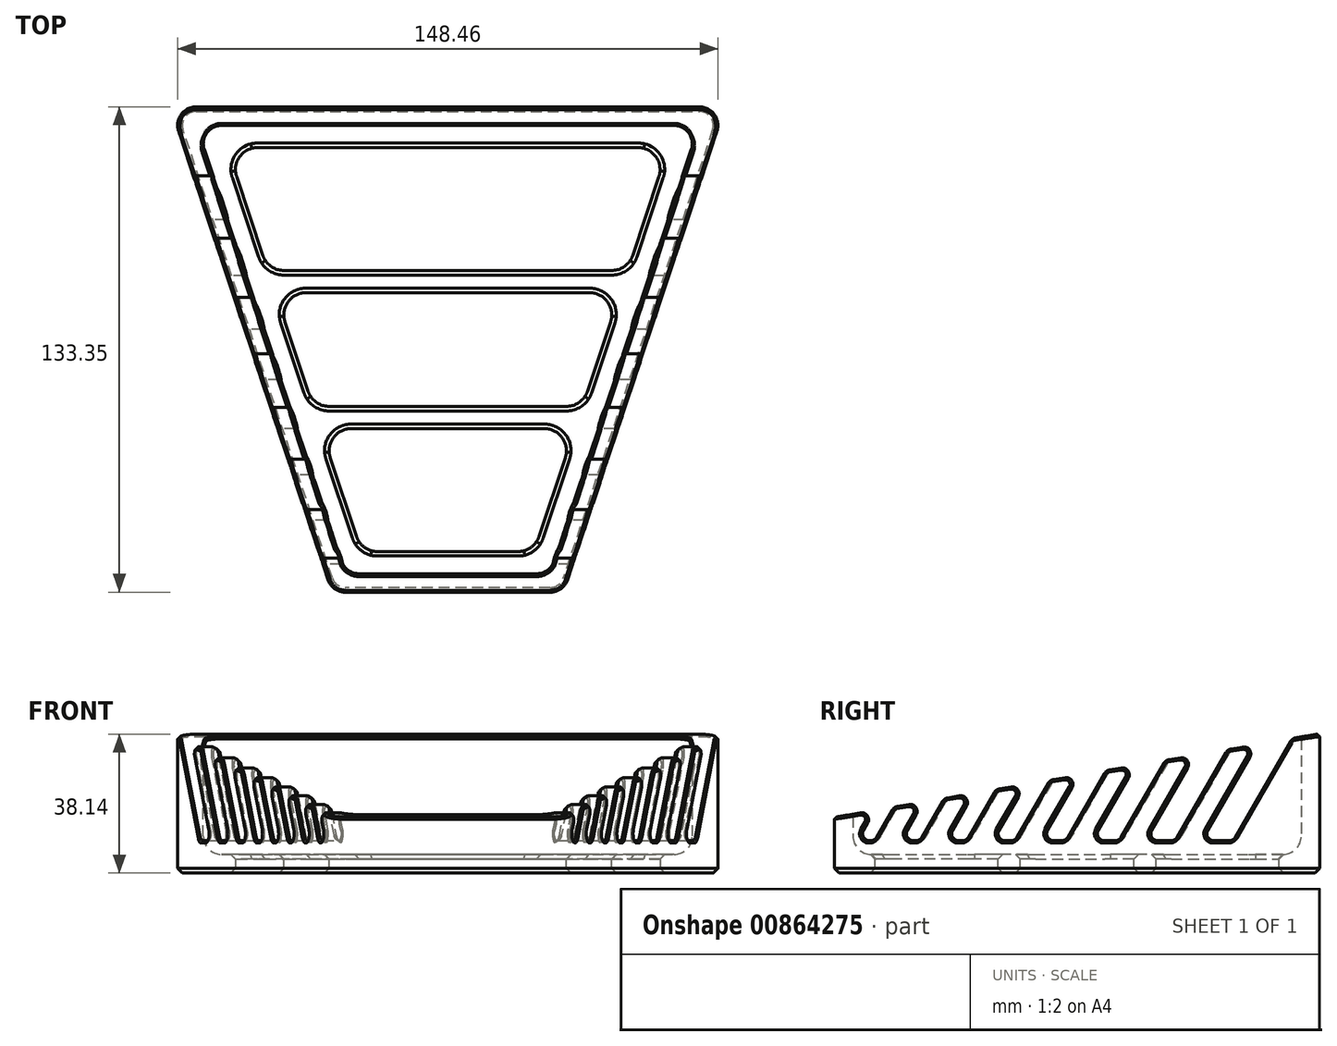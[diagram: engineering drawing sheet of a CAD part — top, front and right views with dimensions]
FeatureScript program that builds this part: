
annotation { "Feature Type Name" : "Feature", "Feature Type Description" : "" }
export const myFeature = defineFeature(function(context is Context, id is Id, definition is map)
    precondition{}
    {
        {
            var Q0;
            Q0=qCreatedBy(makeId("Top.planeOp"),FACE);
            var sketch = newSketch(context, id + "F0", { "sketchPlane" : qUnion([Q0])});
            skLineSegment(sketch, "E0", {"start": v(0, 200.12) * mm, "end": v(0, 0) * mm, "construction": true});
            skLineSegment(sketch, "E1", {"start": v(0, 0) * mm, "end": v(243.38, 0) * mm, "construction": true});
            skLineSegment(sketch, "E2", {"start": v(-76.2, 133.35) * mm, "end": v(76.2, 133.35) * mm});
            skLineSegment(sketch, "E3", {"start": v(76.2, 133.35) * mm, "end": v(31.75, 0) * mm});
            skLineSegment(sketch, "E4", {"start": v(31.75, 0) * mm, "end": v(-31.75, 0) * mm});
            skLineSegment(sketch, "E5", {"start": v(-31.75, 0) * mm, "end": v(-76.2, 133.35) * mm});
            skSolve(sketch);
        }
        {
            var Q0;
            Q0=makeQuery(id+"F0.imprint","IMPRINT",FACE,{"disambiguationData":[TD([[makeQuery(id+"F0.imprint","IMPRINT",EDGE,{"derivedFrom":sQuery(id+"F0.wireOp",EDGE,"E2")}),-1.0]])]});
            extrude(context, id + "F1", {"entities" : qUnion([Q0]), "depth" : 50.8 * mm, "offsetDistance" : 25.4 * mm});
        }
        {
            var Q0;
            Q0=qCreatedBy(makeId("Right.planeOp"),FACE);
            var sketch = newSketch(context, id + "F2", { "sketchPlane" : qUnion([Q0])});
            skLineSegment(sketch, "E6", {"start": v(0, 88.7) * mm, "end": v(0, 0) * mm, "construction": true});
            skLineSegment(sketch, "E7", {"start": v(0, 0) * mm, "end": v(187.78, 0) * mm, "construction": true});
            skCircle(sketch, "E8", {"center": v(118.68, 14.67) * mm, "radius": 14.67 * mm, "construction": true});
            skLineSegment(sketch, "E9", {"start": v(118.68, 14.67) * mm, "end": v(4.95, 4.95) * mm, "construction": true});
            skLineSegment(sketch, "E10", {"start": v(8.28, 1.29) * mm, "end": v(107.5, 5.17) * mm, "construction": true});
            skCircle(sketch, "E11", {"center": v(4.95, 4.95) * mm, "radius": 4.95 * mm, "construction": true});
            skLineSegment(sketch, "E12", {"start": v(116.2, 29.12) * mm, "end": v(4.11, 9.83) * mm, "construction": true});
            skSolve(sketch);
        }
        {
            var Q0;
            Q0=makeQuery(id+"F1.opExtrude","CAP_FACE",FACE,{"disambiguationData":[OSD([sQuery(id+"F0.wireOp",EDGE,"E2"),sQuery(id+"F0.wireOp",EDGE,"E3"),sQuery(id+"F0.wireOp",EDGE,"E4"),sQuery(id+"F0.wireOp",EDGE,"E5")])],"isStart":false});
            shell(context, id + "F3", {"entities" : qUnion([Q0]), "thickness" : 5.08 * mm});
        }
        {
            var Q0;
            Q0=qCreatedBy(makeId("Right.planeOp"),FACE);
            var sketch = newSketch(context, id + "F4", { "sketchPlane" : qUnion([Q0])});
            skLineSegment(sketch, "E13", {"start": v(0, 69.39) * mm, "end": v(0, 0) * mm, "construction": true});
            skLineSegment(sketch, "E14", {"start": v(0, 0) * mm, "end": v(193.07, 0) * mm, "construction": true});
            skLineSegment(sketch, "E15", {"start": v(0, 8.9) * mm, "end": v(186.73, 8.9) * mm, "construction": true});
            skLineSegment(sketch, "E16", {"start": v(-4.36, 14.56) * mm, "end": v(193.37, 48.6) * mm, "construction": true});
            skLineSegment(sketch, "E17", {"start": v(13.77, 17.68) * mm, "end": v(8.7, 8.89) * mm, "construction": true});
            skLineSegment(sketch, "E18", {"start": v(27.37, 20.02) * mm, "end": v(20.94, 8.9) * mm, "construction": true});
            skLineSegment(sketch, "E19", {"start": v(41.37, 22.43) * mm, "end": v(33.55, 8.9) * mm, "construction": true});
            skLineSegment(sketch, "E20", {"start": v(55.86, 24.93) * mm, "end": v(46.6, 8.89) * mm, "construction": true});
            skLineSegment(sketch, "E21", {"start": v(71, 27.53) * mm, "end": v(60.24, 8.89) * mm, "construction": true});
            skLineSegment(sketch, "E22", {"start": v(86.88, 30.27) * mm, "end": v(74.54, 8.89) * mm, "construction": true});
            skLineSegment(sketch, "E23", {"start": v(103.57, 33.14) * mm, "end": v(89.57, 8.89) * mm, "construction": true});
            skLineSegment(sketch, "E24", {"start": v(121, 36.14) * mm, "end": v(105.26, 8.9) * mm, "construction": true});
            skLineSegment(sketch, "E25", {"start": v(125.8, 36.96) * mm, "end": v(146.05, 40.45) * mm});
            skLineSegment(sketch, "E26", {"start": v(146.05, 40.45) * mm, "end": v(146.05, 63.5) * mm});
            skLineSegment(sketch, "E27", {"start": v(146.05, 63.5) * mm, "end": v(-12.7, 63.5) * mm});
            skLineSegment(sketch, "E28", {"start": v(-12.7, 63.5) * mm, "end": v(-12.7, 13.13) * mm});
            skLineSegment(sketch, "E29", {"start": v(-12.7, 13.13) * mm, "end": v(11.17, 17.23) * mm});
            skLineSegment(sketch, "E30", {"start": v(125.8, 36.96) * mm, "end": v(109.59, 8.9) * mm});
            skLineSegment(sketch, "E31", {"start": v(109.59, 8.9) * mm, "end": v(100.94, 8.9) * mm});
            skLineSegment(sketch, "E32", {"start": v(100.94, 8.89) * mm, "end": v(116.2, 35.3) * mm});
            skLineSegment(sketch, "E33", {"start": v(116.2, 35.3) * mm, "end": v(108.05, 33.9) * mm});
            skLineSegment(sketch, "E34", {"start": v(108.05, 33.9) * mm, "end": v(93.6, 8.89) * mm});
            skLineSegment(sketch, "E35", {"start": v(93.6, 8.9) * mm, "end": v(85.54, 8.9) * mm});
            skLineSegment(sketch, "E36", {"start": v(85.54, 8.89) * mm, "end": v(99.1, 32.37) * mm});
            skLineSegment(sketch, "E37", {"start": v(99.1, 32.37) * mm, "end": v(90.95, 30.97) * mm});
            skLineSegment(sketch, "E38", {"start": v(90.95, 30.97) * mm, "end": v(78.2, 8.9) * mm});
            skLineSegment(sketch, "E39", {"start": v(78.2, 8.9) * mm, "end": v(70.87, 8.9) * mm});
            skLineSegment(sketch, "E40", {"start": v(70.87, 8.89) * mm, "end": v(82.81, 29.56) * mm});
            skLineSegment(sketch, "E41", {"start": v(82.81, 29.56) * mm, "end": v(74.67, 28.16) * mm});
            skLineSegment(sketch, "E42", {"start": v(74.67, 28.16) * mm, "end": v(63.54, 8.9) * mm});
            skLineSegment(sketch, "E43", {"start": v(63.54, 8.9) * mm, "end": v(56.94, 8.9) * mm});
            skLineSegment(sketch, "E44", {"start": v(56.94, 8.89) * mm, "end": v(67.34, 26.9) * mm});
            skLineSegment(sketch, "E45", {"start": v(67.34, 26.9) * mm, "end": v(59.2, 25.5) * mm});
            skLineSegment(sketch, "E46", {"start": v(59.2, 25.5) * mm, "end": v(49.61, 8.9) * mm});
            skLineSegment(sketch, "E47", {"start": v(49.61, 8.9) * mm, "end": v(43.6, 8.9) * mm});
            skLineSegment(sketch, "E48", {"start": v(43.6, 8.89) * mm, "end": v(52.53, 24.35) * mm});
            skLineSegment(sketch, "E49", {"start": v(52.53, 24.35) * mm, "end": v(44.38, 22.95) * mm});
            skLineSegment(sketch, "E50", {"start": v(44.38, 22.95) * mm, "end": v(36.27, 8.9) * mm});
            skLineSegment(sketch, "E51", {"start": v(36.27, 8.9) * mm, "end": v(30.84, 8.9) * mm});
            skLineSegment(sketch, "E52", {"start": v(30.84, 8.89) * mm, "end": v(38.36, 21.91) * mm});
            skLineSegment(sketch, "E53", {"start": v(38.36, 21.91) * mm, "end": v(30.22, 20.51) * mm});
            skLineSegment(sketch, "E54", {"start": v(30.22, 20.51) * mm, "end": v(23.5, 8.89) * mm});
            skLineSegment(sketch, "E55", {"start": v(23.5, 8.9) * mm, "end": v(18.38, 8.9) * mm});
            skLineSegment(sketch, "E56", {"start": v(18.38, 8.89) * mm, "end": v(24.52, 19.53) * mm});
            skLineSegment(sketch, "E57", {"start": v(24.52, 19.53) * mm, "end": v(16.38, 18.13) * mm});
            skLineSegment(sketch, "E58", {"start": v(16.38, 18.13) * mm, "end": v(11.04, 8.9) * mm});
            skLineSegment(sketch, "E59", {"start": v(11.04, 8.9) * mm, "end": v(6.35, 8.9) * mm});
            skLineSegment(sketch, "E60", {"start": v(6.35, 8.89) * mm, "end": v(11.17, 17.23) * mm});
            skSolve(sketch);
        }
        {
            var Q0;
            Q0 = qSketchRegion(id + "F4", true);
            extrude(context, id + "F5", {"entities" : qUnion([Q0]), "operationType" : NewBodyOperationType.REMOVE, "endBound" : BoundingType.THROUGH_ALL, "oppositeDirection" : true, "depth" : 25.4 * mm, "offsetDistance" : 25.4 * mm, "hasSecondDirection" : true, "secondDirectionBound" : SecondDirectionBoundingType.THROUGH_ALL, "secondDirectionOppositeDirection" : false, "secondDirectionDepth" : 25.4 * mm});
        }
        {
            var Q0;
            Q0=makeQuery(id+"F3.opShell","OFFSET_FACE",FACE,{"disambiguationData":[OSD([sQuery(id+"F0.wireOp",EDGE,"E2"),sQuery(id+"F0.wireOp",EDGE,"E3"),sQuery(id+"F0.wireOp",EDGE,"E4"),sQuery(id+"F0.wireOp",EDGE,"E5")])]});
            var sketch = newSketch(context, id + "F6", { "sketchPlane" : qUnion([Q0])});
            skLineSegment(sketch, "E61", {"start": v(-151.17, 0) * mm, "end": v(0, 0) * mm, "construction": true});
            skLineSegment(sketch, "E62", {"start": v(0, 0) * mm, "end": v(0, 307.09) * mm, "construction": true});
            skLineSegment(sketch, "E63", {"start": v(-23.7, 11.18) * mm, "end": v(23.7, 11.18) * mm});
            skLineSegment(sketch, "E64", {"start": v(23.7, 11.18) * mm, "end": v(34.96, 44.96) * mm});
            skLineSegment(sketch, "E65", {"start": v(60.7, 122.17) * mm, "end": v(-60.7, 122.17) * mm});
            skLineSegment(sketch, "E66", {"start": v(-60.7, 122.17) * mm, "end": v(-49.43, 88.4) * mm});
            skLineSegment(sketch, "E67", {"start": v(-35.97, 48) * mm, "end": v(35.97, 48) * mm, "construction": true});
            skLineSegment(sketch, "E68", {"start": v(-48.42, 85.34) * mm, "end": v(48.42, 85.34) * mm, "construction": true});
            skLineSegment(sketch, "E69", {"start": v(-34.96, 44.96) * mm, "end": v(34.96, 44.96) * mm});
            skLineSegment(sketch, "E70", {"start": v(-36.99, 51.05) * mm, "end": v(36.99, 51.05) * mm});
            skLineSegment(sketch, "E71", {"start": v(-47.4, 82.3) * mm, "end": v(47.4, 82.3) * mm});
            skLineSegment(sketch, "E72", {"start": v(-49.43, 88.4) * mm, "end": v(49.43, 88.4) * mm});
            skLineSegment(sketch, "E73.trimOffspring", {"start": v(-34.96, 44.96) * mm, "end": v(-23.7, 11.18) * mm});
            skLineSegment(sketch, "E74.trimOffspring", {"start": v(36.99, 51.05) * mm, "end": v(47.4, 82.3) * mm});
            skLineSegment(sketch, "E75.trimOffspring", {"start": v(49.43, 88.4) * mm, "end": v(60.7, 122.17) * mm});
            skLineSegment(sketch, "E76.trimOffspring", {"start": v(-47.4, 82.3) * mm, "end": v(-36.99, 51.05) * mm});
            skSolve(sketch);
        }
        {
            var Q0;
            Q0=makeQuery(id+"F6.imprint","IMPRINT",FACE,{"disambiguationData":[TD([[makeQuery(id+"F6.imprint","IMPRINT",EDGE,{"derivedFrom":sQuery(id+"F6.wireOp",EDGE,"E65")}),1.0]])]});
            var Q1;
            Q1=makeQuery(id+"F6.imprint","IMPRINT",FACE,{"disambiguationData":[TD([[makeQuery(id+"F6.imprint","IMPRINT",EDGE,{"derivedFrom":sQuery(id+"F6.wireOp",EDGE,"E70")}),1.0]])]});
            var Q2;
            Q2=makeQuery(id+"F6.imprint","IMPRINT",FACE,{"disambiguationData":[TD([[makeQuery(id+"F6.imprint","IMPRINT",EDGE,{"derivedFrom":sQuery(id+"F6.wireOp",EDGE,"E63")}),1.0]])]});
            extrude(context, id + "F7", {"entities" : qUnion([Q0, Q1, Q2]), "operationType" : NewBodyOperationType.REMOVE, "endBound" : BoundingType.THROUGH_ALL, "oppositeDirection" : true, "depth" : 25.4 * mm, "offsetDistance" : 25.4 * mm});
        }
        {
            var Q0;
            Q0=makeQuery(id+"F7.boolean.opBoolean","COPY",EDGE,{"derivedFrom":makeQuery(id+"F7.opExtrude","SWEPT_EDGE",EDGE,{"disambiguationData":[OSD([sQuery(id+"F6.wireOp",EDGE,"E65"),sQuery(id+"F6.wireOp",EDGE,"E66")])]})});
            var Q1;
            Q1=makeQuery(id+"F7.boolean.opBoolean","COPY",EDGE,{"derivedFrom":makeQuery(id+"F7.opExtrude","SWEPT_EDGE",EDGE,{"disambiguationData":[OSD([sQuery(id+"F6.wireOp",EDGE,"E65"),sQuery(id+"F6.wireOp",EDGE,"E75.trimOffspring")])]})});
            var Q2;
            Q2=makeQuery(id+"F7.boolean.opBoolean","COPY",EDGE,{"derivedFrom":makeQuery(id+"F7.opExtrude","SWEPT_EDGE",EDGE,{"disambiguationData":[OSD([sQuery(id+"F6.wireOp",EDGE,"E71"),sQuery(id+"F6.wireOp",EDGE,"E74.trimOffspring")])]})});
            var Q3;
            Q3=makeQuery(id+"F7.boolean.opBoolean","COPY",EDGE,{"derivedFrom":makeQuery(id+"F7.opExtrude","SWEPT_EDGE",EDGE,{"disambiguationData":[OSD([sQuery(id+"F6.wireOp",EDGE,"E64"),sQuery(id+"F6.wireOp",EDGE,"E69")])]})});
            var Q4;
            Q4=makeQuery(id+"F7.boolean.opBoolean","COPY",EDGE,{"derivedFrom":makeQuery(id+"F7.opExtrude","SWEPT_EDGE",EDGE,{"disambiguationData":[OSD([sQuery(id+"F6.wireOp",EDGE,"E63"),sQuery(id+"F6.wireOp",EDGE,"E64")])]})});
            var Q5;
            Q5=makeQuery(id+"F7.boolean.opBoolean","COPY",EDGE,{"derivedFrom":makeQuery(id+"F7.opExtrude","SWEPT_EDGE",EDGE,{"disambiguationData":[OSD([sQuery(id+"F6.wireOp",EDGE,"E70"),sQuery(id+"F6.wireOp",EDGE,"E74.trimOffspring")])]})});
            var Q6;
            Q6=makeQuery(id+"F7.boolean.opBoolean","COPY",EDGE,{"derivedFrom":makeQuery(id+"F7.opExtrude","SWEPT_EDGE",EDGE,{"disambiguationData":[OSD([sQuery(id+"F6.wireOp",EDGE,"E72"),sQuery(id+"F6.wireOp",EDGE,"E75.trimOffspring")])]})});
            var Q7;
            Q7=makeQuery(id+"F7.boolean.opBoolean","COPY",EDGE,{"derivedFrom":makeQuery(id+"F7.opExtrude","SWEPT_EDGE",EDGE,{"disambiguationData":[OSD([sQuery(id+"F6.wireOp",EDGE,"E63"),sQuery(id+"F6.wireOp",EDGE,"E73.trimOffspring")])]})});
            var Q8;
            Q8=makeQuery(id+"F7.boolean.opBoolean","COPY",EDGE,{"derivedFrom":makeQuery(id+"F7.opExtrude","SWEPT_EDGE",EDGE,{"disambiguationData":[OSD([sQuery(id+"F6.wireOp",EDGE,"E70"),sQuery(id+"F6.wireOp",EDGE,"E76.trimOffspring")])]})});
            var Q9;
            Q9=makeQuery(id+"F7.boolean.opBoolean","COPY",EDGE,{"derivedFrom":makeQuery(id+"F7.opExtrude","SWEPT_EDGE",EDGE,{"disambiguationData":[OSD([sQuery(id+"F6.wireOp",EDGE,"E66"),sQuery(id+"F6.wireOp",EDGE,"E72")])]})});
            var Q10;
            Q10=makeQuery(id+"F7.boolean.opBoolean","COPY",EDGE,{"derivedFrom":makeQuery(id+"F7.opExtrude","SWEPT_EDGE",EDGE,{"disambiguationData":[OSD([sQuery(id+"F6.wireOp",EDGE,"E71"),sQuery(id+"F6.wireOp",EDGE,"E76.trimOffspring")])]})});
            var Q11;
            Q11=makeQuery(id+"F7.boolean.opBoolean","COPY",EDGE,{"derivedFrom":makeQuery(id+"F7.opExtrude","SWEPT_EDGE",EDGE,{"disambiguationData":[OSD([sQuery(id+"F6.wireOp",EDGE,"E69"),sQuery(id+"F6.wireOp",EDGE,"E73.trimOffspring")])]})});
            fillet(context, id + "F8", {"entities" : qUnion([Q0, Q1, Q2, Q3, Q4, Q5, Q6, Q7, Q8, Q9, Q10, Q11]), "radius" : 6.1 * mm, "tangentPropagation" : true, "allowEdgeOverflow" : false});
        }
        {
            var Q0;
            Q0=makeQuery(id+"F3.opShell","OFFSET_EDGE",EDGE,{"disambiguationData":[OSD([sQuery(id+"F0.wireOp",EDGE,"E2"),sQuery(id+"F0.wireOp",EDGE,"E3")])]});
            var Q1;
            Q1=makeQuery(id+"F3.opShell","OFFSET_EDGE",EDGE,{"disambiguationData":[OSD([sQuery(id+"F0.wireOp",EDGE,"E2"),sQuery(id+"F0.wireOp",EDGE,"E5")])]});
            var Q2;
            Q2=makeQuery(id+"F3.opShell","OFFSET_EDGE",EDGE,{"disambiguationData":[OSD([sQuery(id+"F0.wireOp",EDGE,"E4"),sQuery(id+"F0.wireOp",EDGE,"E5")])]});
            var Q3;
            Q3=makeQuery(id+"F3.opShell","OFFSET_EDGE",EDGE,{"disambiguationData":[OSD([sQuery(id+"F0.wireOp",EDGE,"E3"),sQuery(id+"F0.wireOp",EDGE,"E4")])]});
            var Q4;
            Q4=makeQuery(id+"F1.opExtrude","SWEPT_EDGE",EDGE,{"disambiguationData":[OSD([sQuery(id+"F0.wireOp",EDGE,"E2"),sQuery(id+"F0.wireOp",EDGE,"E5")])]});
            var Q5;
            Q5=makeQuery(id+"F1.opExtrude","SWEPT_EDGE",EDGE,{"disambiguationData":[OSD([sQuery(id+"F0.wireOp",EDGE,"E4"),sQuery(id+"F0.wireOp",EDGE,"E5")])]});
            var Q6;
            Q6=makeQuery(id+"F1.opExtrude","SWEPT_EDGE",EDGE,{"disambiguationData":[OSD([sQuery(id+"F0.wireOp",EDGE,"E3"),sQuery(id+"F0.wireOp",EDGE,"E4")])]});
            var Q7;
            Q7=makeQuery(id+"F1.opExtrude","SWEPT_EDGE",EDGE,{"disambiguationData":[OSD([sQuery(id+"F0.wireOp",EDGE,"E2"),sQuery(id+"F0.wireOp",EDGE,"E3")])]});
            fillet(context, id + "F9", {"entities" : qUnion([Q0, Q1, Q2, Q3, Q4, Q5, Q6, Q7]), "radius" : 5.08 * mm, "tangentPropagation" : true, "allowEdgeOverflow" : false});
        }
        {
            var Q0;
            {var subQ0=sQuery(id+"F0.wireOp",EDGE,"E5");var subQ1=sQuery(id+"F0.wireOp",EDGE,"E2");Q0=makeQuery(id+"F9.opFillet","BLEND_EDGE",EDGE,{"blendedFrom":[makeQuery(id+"F3.opShell","OFFSET_EDGE",EDGE,{"disambiguationData":[OSD([subQ1,subQ0])]}),makeQuery(id+"F3.opShell","OFFSET_FACE",FACE,{"disambiguationData":[OSD([subQ1,sQuery(id+"F0.wireOp",EDGE,"E3"),sQuery(id+"F0.wireOp",EDGE,"E4"),subQ0])]})],"blendedInto":[makeQuery(id+"F3.opShell","OFFSET_FACE",FACE,{"disambiguationData":[OSD([subQ1,sQuery(id+"F0.wireOp",EDGE,"E3"),sQuery(id+"F0.wireOp",EDGE,"E4"),subQ0])]})]});}
            fillet(context, id + "F10", {"entities" : qUnion([Q0]), "radius" : 5.08 * mm, "tangentPropagation" : true, "allowEdgeOverflow" : false});
        }
        {
            var Q0;
            {var subQ0=sQuery(id+"F0.wireOp",EDGE,"E3");var subQ1=sQuery(id+"F4.wireOp",EDGE,"E58");var subQ2=sQuery(id+"F4.wireOp",EDGE,"E59");Q0=makeQuery(id+"F5.boolean.opBoolean","COPY",EDGE,{"disambiguationData":[TD([makeQuery(id+"F1.opExtrude","SWEPT_FACE",FACE,{"disambiguationData":[OSD([subQ0])]})])],"derivedFrom":makeQuery(id+"F5.opExtrude","SWEPT_EDGE",EDGE,{"disambiguationData":[OSD([subQ1,subQ2])]})});}
            var Q1;
            {var subQ0=sQuery(id+"F0.wireOp",EDGE,"E3");var subQ1=sQuery(id+"F4.wireOp",EDGE,"E59");var subQ2=sQuery(id+"F4.wireOp",EDGE,"E60");Q1=makeQuery(id+"F5.boolean.opBoolean","COPY",EDGE,{"disambiguationData":[TD([makeQuery(id+"F1.opExtrude","SWEPT_FACE",FACE,{"disambiguationData":[OSD([subQ0])]})])],"derivedFrom":makeQuery(id+"F5.opExtrude","SWEPT_EDGE",EDGE,{"disambiguationData":[OSD([subQ1,subQ2])]})});}
            var Q2;
            {var subQ0=sQuery(id+"F0.wireOp",EDGE,"E3");var subQ1=sQuery(id+"F4.wireOp",EDGE,"E56");var subQ2=sQuery(id+"F4.wireOp",EDGE,"E55");Q2=makeQuery(id+"F5.boolean.opBoolean","COPY",EDGE,{"disambiguationData":[TD([makeQuery(id+"F1.opExtrude","SWEPT_FACE",FACE,{"disambiguationData":[OSD([subQ0])]})])],"derivedFrom":makeQuery(id+"F5.opExtrude","SWEPT_EDGE",EDGE,{"disambiguationData":[OSD([subQ2,subQ1])]})});}
            var Q3;
            {var subQ0=sQuery(id+"F0.wireOp",EDGE,"E3");var subQ1=sQuery(id+"F4.wireOp",EDGE,"E54");var subQ2=sQuery(id+"F4.wireOp",EDGE,"E55");Q3=makeQuery(id+"F5.boolean.opBoolean","COPY",EDGE,{"disambiguationData":[TD([makeQuery(id+"F1.opExtrude","SWEPT_FACE",FACE,{"disambiguationData":[OSD([subQ0])]})])],"derivedFrom":makeQuery(id+"F5.opExtrude","SWEPT_EDGE",EDGE,{"disambiguationData":[OSD([subQ1,subQ2])]})});}
            var Q4;
            {var subQ0=sQuery(id+"F0.wireOp",EDGE,"E3");var subQ1=sQuery(id+"F4.wireOp",EDGE,"E51");var subQ2=sQuery(id+"F4.wireOp",EDGE,"E50");Q4=makeQuery(id+"F5.boolean.opBoolean","COPY",EDGE,{"disambiguationData":[TD([makeQuery(id+"F1.opExtrude","SWEPT_FACE",FACE,{"disambiguationData":[OSD([subQ0])]})])],"derivedFrom":makeQuery(id+"F5.opExtrude","SWEPT_EDGE",EDGE,{"disambiguationData":[OSD([subQ2,subQ1])]})});}
            var Q5;
            {var subQ0=sQuery(id+"F0.wireOp",EDGE,"E3");var subQ1=sQuery(id+"F4.wireOp",EDGE,"E46");var subQ2=sQuery(id+"F4.wireOp",EDGE,"E47");Q5=makeQuery(id+"F5.boolean.opBoolean","COPY",EDGE,{"disambiguationData":[TD([makeQuery(id+"F1.opExtrude","SWEPT_FACE",FACE,{"disambiguationData":[OSD([subQ0])]})])],"derivedFrom":makeQuery(id+"F5.opExtrude","SWEPT_EDGE",EDGE,{"disambiguationData":[OSD([subQ1,subQ2])]})});}
            var Q6;
            {var subQ0=sQuery(id+"F0.wireOp",EDGE,"E3");var subQ1=sQuery(id+"F4.wireOp",EDGE,"E42");var subQ2=sQuery(id+"F4.wireOp",EDGE,"E43");Q6=makeQuery(id+"F5.boolean.opBoolean","COPY",EDGE,{"disambiguationData":[TD([makeQuery(id+"F1.opExtrude","SWEPT_FACE",FACE,{"disambiguationData":[OSD([subQ0])]})])],"derivedFrom":makeQuery(id+"F5.opExtrude","SWEPT_EDGE",EDGE,{"disambiguationData":[OSD([subQ1,subQ2])]})});}
            var Q7;
            {var subQ0=sQuery(id+"F0.wireOp",EDGE,"E3");var subQ1=sQuery(id+"F4.wireOp",EDGE,"E38");var subQ2=sQuery(id+"F4.wireOp",EDGE,"E39");Q7=makeQuery(id+"F5.boolean.opBoolean","COPY",EDGE,{"disambiguationData":[TD([makeQuery(id+"F1.opExtrude","SWEPT_FACE",FACE,{"disambiguationData":[OSD([subQ0])]})])],"derivedFrom":makeQuery(id+"F5.opExtrude","SWEPT_EDGE",EDGE,{"disambiguationData":[OSD([subQ1,subQ2])]})});}
            var Q8;
            {var subQ0=sQuery(id+"F0.wireOp",EDGE,"E3");var subQ1=sQuery(id+"F4.wireOp",EDGE,"E34");var subQ2=sQuery(id+"F4.wireOp",EDGE,"E35");Q8=makeQuery(id+"F5.boolean.opBoolean","COPY",EDGE,{"disambiguationData":[TD([makeQuery(id+"F1.opExtrude","SWEPT_FACE",FACE,{"disambiguationData":[OSD([subQ0])]})])],"derivedFrom":makeQuery(id+"F5.opExtrude","SWEPT_EDGE",EDGE,{"disambiguationData":[OSD([subQ1,subQ2])]})});}
            var Q9;
            {var subQ0=sQuery(id+"F0.wireOp",EDGE,"E3");var subQ1=sQuery(id+"F4.wireOp",EDGE,"E31");var subQ2=sQuery(id+"F4.wireOp",EDGE,"E30");Q9=makeQuery(id+"F5.boolean.opBoolean","COPY",EDGE,{"disambiguationData":[TD([makeQuery(id+"F1.opExtrude","SWEPT_FACE",FACE,{"disambiguationData":[OSD([subQ0])]})])],"derivedFrom":makeQuery(id+"F5.opExtrude","SWEPT_EDGE",EDGE,{"disambiguationData":[OSD([subQ2,subQ1])]})});}
            var Q10;
            {var subQ0=sQuery(id+"F0.wireOp",EDGE,"E3");var subQ1=sQuery(id+"F4.wireOp",EDGE,"E31");var subQ2=sQuery(id+"F4.wireOp",EDGE,"E32");Q10=makeQuery(id+"F5.boolean.opBoolean","COPY",EDGE,{"disambiguationData":[TD([makeQuery(id+"F1.opExtrude","SWEPT_FACE",FACE,{"disambiguationData":[OSD([subQ0])]})])],"derivedFrom":makeQuery(id+"F5.opExtrude","SWEPT_EDGE",EDGE,{"disambiguationData":[OSD([subQ1,subQ2])]})});}
            var Q11;
            {var subQ0=sQuery(id+"F0.wireOp",EDGE,"E3");var subQ1=sQuery(id+"F4.wireOp",EDGE,"E36");var subQ2=sQuery(id+"F4.wireOp",EDGE,"E35");Q11=makeQuery(id+"F5.boolean.opBoolean","COPY",EDGE,{"disambiguationData":[TD([makeQuery(id+"F1.opExtrude","SWEPT_FACE",FACE,{"disambiguationData":[OSD([subQ0])]})])],"derivedFrom":makeQuery(id+"F5.opExtrude","SWEPT_EDGE",EDGE,{"disambiguationData":[OSD([subQ2,subQ1])]})});}
            var Q12;
            {var subQ0=sQuery(id+"F0.wireOp",EDGE,"E3");var subQ1=sQuery(id+"F4.wireOp",EDGE,"E39");var subQ2=sQuery(id+"F4.wireOp",EDGE,"E40");Q12=makeQuery(id+"F5.boolean.opBoolean","COPY",EDGE,{"disambiguationData":[TD([makeQuery(id+"F1.opExtrude","SWEPT_FACE",FACE,{"disambiguationData":[OSD([subQ0])]})])],"derivedFrom":makeQuery(id+"F5.opExtrude","SWEPT_EDGE",EDGE,{"disambiguationData":[OSD([subQ1,subQ2])]})});}
            var Q13;
            {var subQ0=sQuery(id+"F0.wireOp",EDGE,"E3");var subQ1=sQuery(id+"F4.wireOp",EDGE,"E43");var subQ2=sQuery(id+"F4.wireOp",EDGE,"E44");Q13=makeQuery(id+"F5.boolean.opBoolean","COPY",EDGE,{"disambiguationData":[TD([makeQuery(id+"F1.opExtrude","SWEPT_FACE",FACE,{"disambiguationData":[OSD([subQ0])]})])],"derivedFrom":makeQuery(id+"F5.opExtrude","SWEPT_EDGE",EDGE,{"disambiguationData":[OSD([subQ1,subQ2])]})});}
            var Q14;
            {var subQ0=sQuery(id+"F0.wireOp",EDGE,"E3");var subQ1=sQuery(id+"F4.wireOp",EDGE,"E47");var subQ2=sQuery(id+"F4.wireOp",EDGE,"E48");Q14=makeQuery(id+"F5.boolean.opBoolean","COPY",EDGE,{"disambiguationData":[TD([makeQuery(id+"F1.opExtrude","SWEPT_FACE",FACE,{"disambiguationData":[OSD([subQ0])]})])],"derivedFrom":makeQuery(id+"F5.opExtrude","SWEPT_EDGE",EDGE,{"disambiguationData":[OSD([subQ1,subQ2])]})});}
            var Q15;
            {var subQ0=sQuery(id+"F0.wireOp",EDGE,"E3");var subQ1=sQuery(id+"F4.wireOp",EDGE,"E51");var subQ2=sQuery(id+"F4.wireOp",EDGE,"E52");Q15=makeQuery(id+"F5.boolean.opBoolean","COPY",EDGE,{"disambiguationData":[TD([makeQuery(id+"F1.opExtrude","SWEPT_FACE",FACE,{"disambiguationData":[OSD([subQ0])]})])],"derivedFrom":makeQuery(id+"F5.opExtrude","SWEPT_EDGE",EDGE,{"disambiguationData":[OSD([subQ1,subQ2])]})});}
            var Q16;
            {var subQ0=sQuery(id+"F0.wireOp",EDGE,"E5");var subQ1=sQuery(id+"F4.wireOp",EDGE,"E59");var subQ2=sQuery(id+"F4.wireOp",EDGE,"E60");Q16=makeQuery(id+"F5.boolean.opBoolean","COPY",EDGE,{"disambiguationData":[TD([makeQuery(id+"F1.opExtrude","SWEPT_FACE",FACE,{"disambiguationData":[OSD([subQ0])]})])],"derivedFrom":makeQuery(id+"F5.opExtrude","SWEPT_EDGE",EDGE,{"disambiguationData":[OSD([subQ1,subQ2])]})});}
            var Q17;
            {var subQ0=sQuery(id+"F0.wireOp",EDGE,"E5");var subQ1=sQuery(id+"F4.wireOp",EDGE,"E55");var subQ2=sQuery(id+"F4.wireOp",EDGE,"E56");Q17=makeQuery(id+"F5.boolean.opBoolean","COPY",EDGE,{"disambiguationData":[TD([makeQuery(id+"F1.opExtrude","SWEPT_FACE",FACE,{"disambiguationData":[OSD([subQ0])]})])],"derivedFrom":makeQuery(id+"F5.opExtrude","SWEPT_EDGE",EDGE,{"disambiguationData":[OSD([subQ1,subQ2])]})});}
            var Q18;
            {var subQ0=sQuery(id+"F0.wireOp",EDGE,"E5");var subQ1=sQuery(id+"F4.wireOp",EDGE,"E51");var subQ2=sQuery(id+"F4.wireOp",EDGE,"E52");Q18=makeQuery(id+"F5.boolean.opBoolean","COPY",EDGE,{"disambiguationData":[TD([makeQuery(id+"F1.opExtrude","SWEPT_FACE",FACE,{"disambiguationData":[OSD([subQ0])]})])],"derivedFrom":makeQuery(id+"F5.opExtrude","SWEPT_EDGE",EDGE,{"disambiguationData":[OSD([subQ1,subQ2])]})});}
            var Q19;
            {var subQ0=sQuery(id+"F0.wireOp",EDGE,"E5");var subQ1=sQuery(id+"F4.wireOp",EDGE,"E48");var subQ2=sQuery(id+"F4.wireOp",EDGE,"E47");Q19=makeQuery(id+"F5.boolean.opBoolean","COPY",EDGE,{"disambiguationData":[TD([makeQuery(id+"F1.opExtrude","SWEPT_FACE",FACE,{"disambiguationData":[OSD([subQ0])]})])],"derivedFrom":makeQuery(id+"F5.opExtrude","SWEPT_EDGE",EDGE,{"disambiguationData":[OSD([subQ2,subQ1])]})});}
            var Q20;
            {var subQ0=sQuery(id+"F0.wireOp",EDGE,"E5");var subQ1=sQuery(id+"F4.wireOp",EDGE,"E58");var subQ2=sQuery(id+"F4.wireOp",EDGE,"E59");Q20=makeQuery(id+"F5.boolean.opBoolean","COPY",EDGE,{"disambiguationData":[TD([makeQuery(id+"F1.opExtrude","SWEPT_FACE",FACE,{"disambiguationData":[OSD([subQ0])]})])],"derivedFrom":makeQuery(id+"F5.opExtrude","SWEPT_EDGE",EDGE,{"disambiguationData":[OSD([subQ1,subQ2])]})});}
            var Q21;
            {var subQ0=sQuery(id+"F0.wireOp",EDGE,"E5");var subQ1=sQuery(id+"F4.wireOp",EDGE,"E54");var subQ2=sQuery(id+"F4.wireOp",EDGE,"E55");Q21=makeQuery(id+"F5.boolean.opBoolean","COPY",EDGE,{"disambiguationData":[TD([makeQuery(id+"F1.opExtrude","SWEPT_FACE",FACE,{"disambiguationData":[OSD([subQ0])]})])],"derivedFrom":makeQuery(id+"F5.opExtrude","SWEPT_EDGE",EDGE,{"disambiguationData":[OSD([subQ1,subQ2])]})});}
            var Q22;
            {var subQ0=sQuery(id+"F0.wireOp",EDGE,"E5");var subQ1=sQuery(id+"F4.wireOp",EDGE,"E50");var subQ2=sQuery(id+"F4.wireOp",EDGE,"E51");Q22=makeQuery(id+"F5.boolean.opBoolean","COPY",EDGE,{"disambiguationData":[TD([makeQuery(id+"F1.opExtrude","SWEPT_FACE",FACE,{"disambiguationData":[OSD([subQ0])]})])],"derivedFrom":makeQuery(id+"F5.opExtrude","SWEPT_EDGE",EDGE,{"disambiguationData":[OSD([subQ1,subQ2])]})});}
            var Q23;
            {var subQ0=sQuery(id+"F0.wireOp",EDGE,"E5");var subQ1=sQuery(id+"F4.wireOp",EDGE,"E46");var subQ2=sQuery(id+"F4.wireOp",EDGE,"E47");Q23=makeQuery(id+"F5.boolean.opBoolean","COPY",EDGE,{"disambiguationData":[TD([makeQuery(id+"F1.opExtrude","SWEPT_FACE",FACE,{"disambiguationData":[OSD([subQ0])]})])],"derivedFrom":makeQuery(id+"F5.opExtrude","SWEPT_EDGE",EDGE,{"disambiguationData":[OSD([subQ1,subQ2])]})});}
            var Q24;
            {var subQ0=sQuery(id+"F0.wireOp",EDGE,"E5");var subQ1=sQuery(id+"F4.wireOp",EDGE,"E43");var subQ2=sQuery(id+"F4.wireOp",EDGE,"E42");Q24=makeQuery(id+"F5.boolean.opBoolean","COPY",EDGE,{"disambiguationData":[TD([makeQuery(id+"F1.opExtrude","SWEPT_FACE",FACE,{"disambiguationData":[OSD([subQ0])]})])],"derivedFrom":makeQuery(id+"F5.opExtrude","SWEPT_EDGE",EDGE,{"disambiguationData":[OSD([subQ2,subQ1])]})});}
            var Q25;
            {var subQ0=sQuery(id+"F0.wireOp",EDGE,"E5");var subQ1=sQuery(id+"F4.wireOp",EDGE,"E43");var subQ2=sQuery(id+"F4.wireOp",EDGE,"E44");Q25=makeQuery(id+"F5.boolean.opBoolean","COPY",EDGE,{"disambiguationData":[TD([makeQuery(id+"F1.opExtrude","SWEPT_FACE",FACE,{"disambiguationData":[OSD([subQ0])]})])],"derivedFrom":makeQuery(id+"F5.opExtrude","SWEPT_EDGE",EDGE,{"disambiguationData":[OSD([subQ1,subQ2])]})});}
            var Q26;
            {var subQ0=sQuery(id+"F0.wireOp",EDGE,"E5");var subQ1=sQuery(id+"F4.wireOp",EDGE,"E39");var subQ2=sQuery(id+"F4.wireOp",EDGE,"E40");Q26=makeQuery(id+"F5.boolean.opBoolean","COPY",EDGE,{"disambiguationData":[TD([makeQuery(id+"F1.opExtrude","SWEPT_FACE",FACE,{"disambiguationData":[OSD([subQ0])]})])],"derivedFrom":makeQuery(id+"F5.opExtrude","SWEPT_EDGE",EDGE,{"disambiguationData":[OSD([subQ1,subQ2])]})});}
            var Q27;
            {var subQ0=sQuery(id+"F0.wireOp",EDGE,"E5");var subQ1=sQuery(id+"F4.wireOp",EDGE,"E38");var subQ2=sQuery(id+"F4.wireOp",EDGE,"E39");Q27=makeQuery(id+"F5.boolean.opBoolean","COPY",EDGE,{"disambiguationData":[TD([makeQuery(id+"F1.opExtrude","SWEPT_FACE",FACE,{"disambiguationData":[OSD([subQ0])]})])],"derivedFrom":makeQuery(id+"F5.opExtrude","SWEPT_EDGE",EDGE,{"disambiguationData":[OSD([subQ1,subQ2])]})});}
            var Q28;
            {var subQ0=sQuery(id+"F0.wireOp",EDGE,"E5");var subQ1=sQuery(id+"F4.wireOp",EDGE,"E35");var subQ2=sQuery(id+"F4.wireOp",EDGE,"E36");Q28=makeQuery(id+"F5.boolean.opBoolean","COPY",EDGE,{"disambiguationData":[TD([makeQuery(id+"F1.opExtrude","SWEPT_FACE",FACE,{"disambiguationData":[OSD([subQ0])]})])],"derivedFrom":makeQuery(id+"F5.opExtrude","SWEPT_EDGE",EDGE,{"disambiguationData":[OSD([subQ1,subQ2])]})});}
            var Q29;
            {var subQ0=sQuery(id+"F0.wireOp",EDGE,"E5");var subQ1=sQuery(id+"F4.wireOp",EDGE,"E34");var subQ2=sQuery(id+"F4.wireOp",EDGE,"E35");Q29=makeQuery(id+"F5.boolean.opBoolean","COPY",EDGE,{"disambiguationData":[TD([makeQuery(id+"F1.opExtrude","SWEPT_FACE",FACE,{"disambiguationData":[OSD([subQ0])]})])],"derivedFrom":makeQuery(id+"F5.opExtrude","SWEPT_EDGE",EDGE,{"disambiguationData":[OSD([subQ1,subQ2])]})});}
            var Q30;
            {var subQ0=sQuery(id+"F0.wireOp",EDGE,"E5");var subQ1=sQuery(id+"F4.wireOp",EDGE,"E30");var subQ2=sQuery(id+"F4.wireOp",EDGE,"E31");Q30=makeQuery(id+"F5.boolean.opBoolean","COPY",EDGE,{"disambiguationData":[TD([makeQuery(id+"F1.opExtrude","SWEPT_FACE",FACE,{"disambiguationData":[OSD([subQ0])]})])],"derivedFrom":makeQuery(id+"F5.opExtrude","SWEPT_EDGE",EDGE,{"disambiguationData":[OSD([subQ1,subQ2])]})});}
            var Q31;
            {var subQ0=sQuery(id+"F0.wireOp",EDGE,"E5");var subQ1=sQuery(id+"F4.wireOp",EDGE,"E31");var subQ2=sQuery(id+"F4.wireOp",EDGE,"E32");Q31=makeQuery(id+"F5.boolean.opBoolean","COPY",EDGE,{"disambiguationData":[TD([makeQuery(id+"F1.opExtrude","SWEPT_FACE",FACE,{"disambiguationData":[OSD([subQ0])]})])],"derivedFrom":makeQuery(id+"F5.opExtrude","SWEPT_EDGE",EDGE,{"disambiguationData":[OSD([subQ1,subQ2])]})});}
            fillet(context, id + "F11", {"entities" : qUnion([Q0, Q1, Q2, Q3, Q4, Q5, Q6, Q7, Q8, Q9, Q10, Q11, Q12, Q13, Q14, Q15, Q16, Q17, Q18, Q19, Q20, Q21, Q22, Q23, Q24, Q25, Q26, Q27, Q28, Q29, Q30, Q31]), "radius" : 1.9 * mm, "tangentPropagation" : true, "allowEdgeOverflow" : false});
        }
        {
            var Q0;
            {var subQ0=sQuery(id+"F0.wireOp",EDGE,"E3");var subQ1=sQuery(id+"F4.wireOp",EDGE,"E29");var subQ2=sQuery(id+"F4.wireOp",EDGE,"E60");Q0=makeQuery(id+"F5.boolean.opBoolean","COPY",EDGE,{"disambiguationData":[TD([makeQuery(id+"F1.opExtrude","SWEPT_FACE",FACE,{"disambiguationData":[OSD([subQ0])]})])],"derivedFrom":makeQuery(id+"F5.opExtrude","SWEPT_EDGE",EDGE,{"disambiguationData":[OSD([subQ1,subQ2])]})});}
            var Q1;
            {var subQ0=sQuery(id+"F0.wireOp",EDGE,"E3");var subQ1=sQuery(id+"F4.wireOp",EDGE,"E57");var subQ2=sQuery(id+"F4.wireOp",EDGE,"E58");Q1=makeQuery(id+"F5.boolean.opBoolean","COPY",EDGE,{"disambiguationData":[TD([makeQuery(id+"F1.opExtrude","SWEPT_FACE",FACE,{"disambiguationData":[OSD([subQ0])]})])],"derivedFrom":makeQuery(id+"F5.opExtrude","SWEPT_EDGE",EDGE,{"disambiguationData":[OSD([subQ1,subQ2])]})});}
            var Q2;
            {var subQ0=sQuery(id+"F0.wireOp",EDGE,"E5");var subQ1=sQuery(id+"F4.wireOp",EDGE,"E29");var subQ2=sQuery(id+"F4.wireOp",EDGE,"E60");Q2=makeQuery(id+"F5.boolean.opBoolean","COPY",EDGE,{"disambiguationData":[TD([makeQuery(id+"F1.opExtrude","SWEPT_FACE",FACE,{"disambiguationData":[OSD([subQ0])]})])],"derivedFrom":makeQuery(id+"F5.opExtrude","SWEPT_EDGE",EDGE,{"disambiguationData":[OSD([subQ1,subQ2])]})});}
            var Q3;
            {var subQ0=sQuery(id+"F0.wireOp",EDGE,"E5");var subQ1=sQuery(id+"F4.wireOp",EDGE,"E58");var subQ2=sQuery(id+"F4.wireOp",EDGE,"E57");Q3=makeQuery(id+"F5.boolean.opBoolean","COPY",EDGE,{"disambiguationData":[TD([makeQuery(id+"F1.opExtrude","SWEPT_FACE",FACE,{"disambiguationData":[OSD([subQ0])]})])],"derivedFrom":makeQuery(id+"F5.opExtrude","SWEPT_EDGE",EDGE,{"disambiguationData":[OSD([subQ2,subQ1])]})});}
            var Q4;
            {var subQ0=sQuery(id+"F0.wireOp",EDGE,"E5");var subQ1=sQuery(id+"F4.wireOp",EDGE,"E56");var subQ2=sQuery(id+"F4.wireOp",EDGE,"E57");Q4=makeQuery(id+"F5.boolean.opBoolean","COPY",EDGE,{"disambiguationData":[TD([makeQuery(id+"F1.opExtrude","SWEPT_FACE",FACE,{"disambiguationData":[OSD([subQ0])]})])],"derivedFrom":makeQuery(id+"F5.opExtrude","SWEPT_EDGE",EDGE,{"disambiguationData":[OSD([subQ1,subQ2])]})});}
            var Q5;
            {var subQ0=sQuery(id+"F0.wireOp",EDGE,"E5");var subQ1=sQuery(id+"F4.wireOp",EDGE,"E53");var subQ2=sQuery(id+"F4.wireOp",EDGE,"E54");Q5=makeQuery(id+"F5.boolean.opBoolean","COPY",EDGE,{"disambiguationData":[TD([makeQuery(id+"F1.opExtrude","SWEPT_FACE",FACE,{"disambiguationData":[OSD([subQ0])]})])],"derivedFrom":makeQuery(id+"F5.opExtrude","SWEPT_EDGE",EDGE,{"disambiguationData":[OSD([subQ1,subQ2])]})});}
            var Q6;
            {var subQ0=sQuery(id+"F0.wireOp",EDGE,"E5");var subQ1=sQuery(id+"F4.wireOp",EDGE,"E53");var subQ2=sQuery(id+"F4.wireOp",EDGE,"E52");Q6=makeQuery(id+"F5.boolean.opBoolean","COPY",EDGE,{"disambiguationData":[TD([makeQuery(id+"F1.opExtrude","SWEPT_FACE",FACE,{"disambiguationData":[OSD([subQ0])]})])],"derivedFrom":makeQuery(id+"F5.opExtrude","SWEPT_EDGE",EDGE,{"disambiguationData":[OSD([subQ2,subQ1])]})});}
            var Q7;
            {var subQ0=sQuery(id+"F0.wireOp",EDGE,"E5");var subQ1=sQuery(id+"F4.wireOp",EDGE,"E49");var subQ2=sQuery(id+"F4.wireOp",EDGE,"E50");Q7=makeQuery(id+"F5.boolean.opBoolean","COPY",EDGE,{"disambiguationData":[TD([makeQuery(id+"F1.opExtrude","SWEPT_FACE",FACE,{"disambiguationData":[OSD([subQ0])]})])],"derivedFrom":makeQuery(id+"F5.opExtrude","SWEPT_EDGE",EDGE,{"disambiguationData":[OSD([subQ1,subQ2])]})});}
            var Q8;
            {var subQ0=sQuery(id+"F0.wireOp",EDGE,"E5");var subQ1=sQuery(id+"F4.wireOp",EDGE,"E48");var subQ2=sQuery(id+"F4.wireOp",EDGE,"E49");Q8=makeQuery(id+"F5.boolean.opBoolean","COPY",EDGE,{"disambiguationData":[TD([makeQuery(id+"F1.opExtrude","SWEPT_FACE",FACE,{"disambiguationData":[OSD([subQ0])]})])],"derivedFrom":makeQuery(id+"F5.opExtrude","SWEPT_EDGE",EDGE,{"disambiguationData":[OSD([subQ1,subQ2])]})});}
            var Q9;
            {var subQ0=sQuery(id+"F0.wireOp",EDGE,"E5");var subQ1=sQuery(id+"F4.wireOp",EDGE,"E45");var subQ2=sQuery(id+"F4.wireOp",EDGE,"E46");Q9=makeQuery(id+"F5.boolean.opBoolean","COPY",EDGE,{"disambiguationData":[TD([makeQuery(id+"F1.opExtrude","SWEPT_FACE",FACE,{"disambiguationData":[OSD([subQ0])]})])],"derivedFrom":makeQuery(id+"F5.opExtrude","SWEPT_EDGE",EDGE,{"disambiguationData":[OSD([subQ1,subQ2])]})});}
            var Q10;
            {var subQ0=sQuery(id+"F0.wireOp",EDGE,"E5");var subQ1=sQuery(id+"F4.wireOp",EDGE,"E44");var subQ2=sQuery(id+"F4.wireOp",EDGE,"E45");Q10=makeQuery(id+"F5.boolean.opBoolean","COPY",EDGE,{"disambiguationData":[TD([makeQuery(id+"F1.opExtrude","SWEPT_FACE",FACE,{"disambiguationData":[OSD([subQ0])]})])],"derivedFrom":makeQuery(id+"F5.opExtrude","SWEPT_EDGE",EDGE,{"disambiguationData":[OSD([subQ1,subQ2])]})});}
            var Q11;
            {var subQ0=sQuery(id+"F0.wireOp",EDGE,"E5");var subQ1=sQuery(id+"F4.wireOp",EDGE,"E41");var subQ2=sQuery(id+"F4.wireOp",EDGE,"E42");Q11=makeQuery(id+"F5.boolean.opBoolean","COPY",EDGE,{"disambiguationData":[TD([makeQuery(id+"F1.opExtrude","SWEPT_FACE",FACE,{"disambiguationData":[OSD([subQ0])]})])],"derivedFrom":makeQuery(id+"F5.opExtrude","SWEPT_EDGE",EDGE,{"disambiguationData":[OSD([subQ1,subQ2])]})});}
            var Q12;
            {var subQ0=sQuery(id+"F0.wireOp",EDGE,"E5");var subQ1=sQuery(id+"F4.wireOp",EDGE,"E40");var subQ2=sQuery(id+"F4.wireOp",EDGE,"E41");Q12=makeQuery(id+"F5.boolean.opBoolean","COPY",EDGE,{"disambiguationData":[TD([makeQuery(id+"F1.opExtrude","SWEPT_FACE",FACE,{"disambiguationData":[OSD([subQ0])]})])],"derivedFrom":makeQuery(id+"F5.opExtrude","SWEPT_EDGE",EDGE,{"disambiguationData":[OSD([subQ1,subQ2])]})});}
            var Q13;
            {var subQ0=sQuery(id+"F0.wireOp",EDGE,"E5");var subQ1=sQuery(id+"F4.wireOp",EDGE,"E38");var subQ2=sQuery(id+"F4.wireOp",EDGE,"E37");Q13=makeQuery(id+"F5.boolean.opBoolean","COPY",EDGE,{"disambiguationData":[TD([makeQuery(id+"F1.opExtrude","SWEPT_FACE",FACE,{"disambiguationData":[OSD([subQ0])]})])],"derivedFrom":makeQuery(id+"F5.opExtrude","SWEPT_EDGE",EDGE,{"disambiguationData":[OSD([subQ2,subQ1])]})});}
            var Q14;
            {var subQ0=sQuery(id+"F0.wireOp",EDGE,"E5");var subQ1=sQuery(id+"F4.wireOp",EDGE,"E36");var subQ2=sQuery(id+"F4.wireOp",EDGE,"E37");Q14=makeQuery(id+"F5.boolean.opBoolean","COPY",EDGE,{"disambiguationData":[TD([makeQuery(id+"F1.opExtrude","SWEPT_FACE",FACE,{"disambiguationData":[OSD([subQ0])]})])],"derivedFrom":makeQuery(id+"F5.opExtrude","SWEPT_EDGE",EDGE,{"disambiguationData":[OSD([subQ1,subQ2])]})});}
            var Q15;
            {var subQ0=sQuery(id+"F0.wireOp",EDGE,"E5");var subQ1=sQuery(id+"F4.wireOp",EDGE,"E33");var subQ2=sQuery(id+"F4.wireOp",EDGE,"E34");Q15=makeQuery(id+"F5.boolean.opBoolean","COPY",EDGE,{"disambiguationData":[TD([makeQuery(id+"F1.opExtrude","SWEPT_FACE",FACE,{"disambiguationData":[OSD([subQ0])]})])],"derivedFrom":makeQuery(id+"F5.opExtrude","SWEPT_EDGE",EDGE,{"disambiguationData":[OSD([subQ1,subQ2])]})});}
            var Q16;
            {var subQ0=sQuery(id+"F0.wireOp",EDGE,"E5");var subQ1=sQuery(id+"F4.wireOp",EDGE,"E33");var subQ2=sQuery(id+"F4.wireOp",EDGE,"E32");Q16=makeQuery(id+"F5.boolean.opBoolean","COPY",EDGE,{"disambiguationData":[TD([makeQuery(id+"F1.opExtrude","SWEPT_FACE",FACE,{"disambiguationData":[OSD([subQ0])]})])],"derivedFrom":makeQuery(id+"F5.opExtrude","SWEPT_EDGE",EDGE,{"disambiguationData":[OSD([subQ2,subQ1])]})});}
            var Q17;
            {var subQ0=sQuery(id+"F0.wireOp",EDGE,"E5");var subQ1=sQuery(id+"F4.wireOp",EDGE,"E25");var subQ2=sQuery(id+"F4.wireOp",EDGE,"E30");Q17=makeQuery(id+"F5.boolean.opBoolean","COPY",EDGE,{"disambiguationData":[TD([makeQuery(id+"F1.opExtrude","SWEPT_FACE",FACE,{"disambiguationData":[OSD([subQ0])]})])],"derivedFrom":makeQuery(id+"F5.opExtrude","SWEPT_EDGE",EDGE,{"disambiguationData":[OSD([subQ1,subQ2])]})});}
            var Q18;
            {var subQ0=sQuery(id+"F0.wireOp",EDGE,"E3");var subQ1=sQuery(id+"F4.wireOp",EDGE,"E25");var subQ2=sQuery(id+"F4.wireOp",EDGE,"E30");Q18=makeQuery(id+"F5.boolean.opBoolean","COPY",EDGE,{"disambiguationData":[TD([makeQuery(id+"F1.opExtrude","SWEPT_FACE",FACE,{"disambiguationData":[OSD([subQ0])]})])],"derivedFrom":makeQuery(id+"F5.opExtrude","SWEPT_EDGE",EDGE,{"disambiguationData":[OSD([subQ1,subQ2])]})});}
            var Q19;
            {var subQ0=sQuery(id+"F0.wireOp",EDGE,"E3");var subQ1=sQuery(id+"F4.wireOp",EDGE,"E32");var subQ2=sQuery(id+"F4.wireOp",EDGE,"E33");Q19=makeQuery(id+"F5.boolean.opBoolean","COPY",EDGE,{"disambiguationData":[TD([makeQuery(id+"F1.opExtrude","SWEPT_FACE",FACE,{"disambiguationData":[OSD([subQ0])]})])],"derivedFrom":makeQuery(id+"F5.opExtrude","SWEPT_EDGE",EDGE,{"disambiguationData":[OSD([subQ1,subQ2])]})});}
            var Q20;
            {var subQ0=sQuery(id+"F0.wireOp",EDGE,"E3");var subQ1=sQuery(id+"F4.wireOp",EDGE,"E33");var subQ2=sQuery(id+"F4.wireOp",EDGE,"E34");Q20=makeQuery(id+"F5.boolean.opBoolean","COPY",EDGE,{"disambiguationData":[TD([makeQuery(id+"F1.opExtrude","SWEPT_FACE",FACE,{"disambiguationData":[OSD([subQ0])]})])],"derivedFrom":makeQuery(id+"F5.opExtrude","SWEPT_EDGE",EDGE,{"disambiguationData":[OSD([subQ1,subQ2])]})});}
            var Q21;
            {var subQ0=sQuery(id+"F0.wireOp",EDGE,"E3");var subQ1=sQuery(id+"F4.wireOp",EDGE,"E36");var subQ2=sQuery(id+"F4.wireOp",EDGE,"E37");Q21=makeQuery(id+"F5.boolean.opBoolean","COPY",EDGE,{"disambiguationData":[TD([makeQuery(id+"F1.opExtrude","SWEPT_FACE",FACE,{"disambiguationData":[OSD([subQ0])]})])],"derivedFrom":makeQuery(id+"F5.opExtrude","SWEPT_EDGE",EDGE,{"disambiguationData":[OSD([subQ1,subQ2])]})});}
            var Q22;
            {var subQ0=sQuery(id+"F0.wireOp",EDGE,"E3");var subQ1=sQuery(id+"F4.wireOp",EDGE,"E37");var subQ2=sQuery(id+"F4.wireOp",EDGE,"E38");Q22=makeQuery(id+"F5.boolean.opBoolean","COPY",EDGE,{"disambiguationData":[TD([makeQuery(id+"F1.opExtrude","SWEPT_FACE",FACE,{"disambiguationData":[OSD([subQ0])]})])],"derivedFrom":makeQuery(id+"F5.opExtrude","SWEPT_EDGE",EDGE,{"disambiguationData":[OSD([subQ1,subQ2])]})});}
            var Q23;
            {var subQ0=sQuery(id+"F0.wireOp",EDGE,"E3");var subQ1=sQuery(id+"F4.wireOp",EDGE,"E41");var subQ2=sQuery(id+"F4.wireOp",EDGE,"E40");Q23=makeQuery(id+"F5.boolean.opBoolean","COPY",EDGE,{"disambiguationData":[TD([makeQuery(id+"F1.opExtrude","SWEPT_FACE",FACE,{"disambiguationData":[OSD([subQ0])]})])],"derivedFrom":makeQuery(id+"F5.opExtrude","SWEPT_EDGE",EDGE,{"disambiguationData":[OSD([subQ2,subQ1])]})});}
            var Q24;
            {var subQ0=sQuery(id+"F0.wireOp",EDGE,"E3");var subQ1=sQuery(id+"F4.wireOp",EDGE,"E41");var subQ2=sQuery(id+"F4.wireOp",EDGE,"E42");Q24=makeQuery(id+"F5.boolean.opBoolean","COPY",EDGE,{"disambiguationData":[TD([makeQuery(id+"F1.opExtrude","SWEPT_FACE",FACE,{"disambiguationData":[OSD([subQ0])]})])],"derivedFrom":makeQuery(id+"F5.opExtrude","SWEPT_EDGE",EDGE,{"disambiguationData":[OSD([subQ1,subQ2])]})});}
            var Q25;
            {var subQ0=sQuery(id+"F0.wireOp",EDGE,"E3");var subQ1=sQuery(id+"F4.wireOp",EDGE,"E44");var subQ2=sQuery(id+"F4.wireOp",EDGE,"E45");Q25=makeQuery(id+"F5.boolean.opBoolean","COPY",EDGE,{"disambiguationData":[TD([makeQuery(id+"F1.opExtrude","SWEPT_FACE",FACE,{"disambiguationData":[OSD([subQ0])]})])],"derivedFrom":makeQuery(id+"F5.opExtrude","SWEPT_EDGE",EDGE,{"disambiguationData":[OSD([subQ1,subQ2])]})});}
            var Q26;
            {var subQ0=sQuery(id+"F0.wireOp",EDGE,"E3");var subQ1=sQuery(id+"F4.wireOp",EDGE,"E46");var subQ2=sQuery(id+"F4.wireOp",EDGE,"E45");Q26=makeQuery(id+"F5.boolean.opBoolean","COPY",EDGE,{"disambiguationData":[TD([makeQuery(id+"F1.opExtrude","SWEPT_FACE",FACE,{"disambiguationData":[OSD([subQ0])]})])],"derivedFrom":makeQuery(id+"F5.opExtrude","SWEPT_EDGE",EDGE,{"disambiguationData":[OSD([subQ2,subQ1])]})});}
            var Q27;
            {var subQ0=sQuery(id+"F0.wireOp",EDGE,"E3");var subQ1=sQuery(id+"F4.wireOp",EDGE,"E48");var subQ2=sQuery(id+"F4.wireOp",EDGE,"E49");Q27=makeQuery(id+"F5.boolean.opBoolean","COPY",EDGE,{"disambiguationData":[TD([makeQuery(id+"F1.opExtrude","SWEPT_FACE",FACE,{"disambiguationData":[OSD([subQ0])]})])],"derivedFrom":makeQuery(id+"F5.opExtrude","SWEPT_EDGE",EDGE,{"disambiguationData":[OSD([subQ1,subQ2])]})});}
            var Q28;
            {var subQ0=sQuery(id+"F0.wireOp",EDGE,"E3");var subQ1=sQuery(id+"F4.wireOp",EDGE,"E49");var subQ2=sQuery(id+"F4.wireOp",EDGE,"E50");Q28=makeQuery(id+"F5.boolean.opBoolean","COPY",EDGE,{"disambiguationData":[TD([makeQuery(id+"F1.opExtrude","SWEPT_FACE",FACE,{"disambiguationData":[OSD([subQ0])]})])],"derivedFrom":makeQuery(id+"F5.opExtrude","SWEPT_EDGE",EDGE,{"disambiguationData":[OSD([subQ1,subQ2])]})});}
            var Q29;
            {var subQ0=sQuery(id+"F0.wireOp",EDGE,"E3");var subQ1=sQuery(id+"F4.wireOp",EDGE,"E52");var subQ2=sQuery(id+"F4.wireOp",EDGE,"E53");Q29=makeQuery(id+"F5.boolean.opBoolean","COPY",EDGE,{"disambiguationData":[TD([makeQuery(id+"F1.opExtrude","SWEPT_FACE",FACE,{"disambiguationData":[OSD([subQ0])]})])],"derivedFrom":makeQuery(id+"F5.opExtrude","SWEPT_EDGE",EDGE,{"disambiguationData":[OSD([subQ1,subQ2])]})});}
            var Q30;
            {var subQ0=sQuery(id+"F0.wireOp",EDGE,"E3");var subQ1=sQuery(id+"F4.wireOp",EDGE,"E53");var subQ2=sQuery(id+"F4.wireOp",EDGE,"E54");Q30=makeQuery(id+"F5.boolean.opBoolean","COPY",EDGE,{"disambiguationData":[TD([makeQuery(id+"F1.opExtrude","SWEPT_FACE",FACE,{"disambiguationData":[OSD([subQ0])]})])],"derivedFrom":makeQuery(id+"F5.opExtrude","SWEPT_EDGE",EDGE,{"disambiguationData":[OSD([subQ1,subQ2])]})});}
            var Q31;
            {var subQ0=sQuery(id+"F0.wireOp",EDGE,"E3");var subQ1=sQuery(id+"F4.wireOp",EDGE,"E56");var subQ2=sQuery(id+"F4.wireOp",EDGE,"E57");Q31=makeQuery(id+"F5.boolean.opBoolean","COPY",EDGE,{"disambiguationData":[TD([makeQuery(id+"F1.opExtrude","SWEPT_FACE",FACE,{"disambiguationData":[OSD([subQ0])]})])],"derivedFrom":makeQuery(id+"F5.opExtrude","SWEPT_EDGE",EDGE,{"disambiguationData":[OSD([subQ1,subQ2])]})});}
            fillet(context, id + "F12", {"entities" : qUnion([Q0, Q1, Q2, Q3, Q4, Q5, Q6, Q7, Q8, Q9, Q10, Q11, Q12, Q13, Q14, Q15, Q16, Q17, Q18, Q19, Q20, Q21, Q22, Q23, Q24, Q25, Q26, Q27, Q28, Q29, Q30, Q31]), "radius" : 1.9 * mm, "tangentPropagation" : true, "allowEdgeOverflow" : false});
        }
        {
            var Q0;
            Q0=makeQuery(id+"F8.opFillet","BLEND_EDGE",EDGE,{"blendedFrom":[makeQuery(id+"F7.boolean.opBoolean","COPY",EDGE,{"derivedFrom":makeQuery(id+"F7.opExtrude","SWEPT_EDGE",EDGE,{"disambiguationData":[OSD([sQuery(id+"F6.wireOp",EDGE,"E65"),sQuery(id+"F6.wireOp",EDGE,"E66")])]})}),makeQuery(id+"F3.opShell","OFFSET_FACE",FACE,{"disambiguationData":[OSD([sQuery(id+"F0.wireOp",EDGE,"E2"),sQuery(id+"F0.wireOp",EDGE,"E3"),sQuery(id+"F0.wireOp",EDGE,"E4"),sQuery(id+"F0.wireOp",EDGE,"E5")])]})],"blendedInto":[makeQuery(id+"F3.opShell","OFFSET_FACE",FACE,{"disambiguationData":[OSD([sQuery(id+"F0.wireOp",EDGE,"E2"),sQuery(id+"F0.wireOp",EDGE,"E3"),sQuery(id+"F0.wireOp",EDGE,"E4"),sQuery(id+"F0.wireOp",EDGE,"E5")])]})]});
            var Q1;
            Q1=makeQuery(id+"F8.opFillet","BLEND_EDGE",EDGE,{"blendedFrom":[makeQuery(id+"F7.boolean.opBoolean","COPY",EDGE,{"derivedFrom":makeQuery(id+"F7.opExtrude","SWEPT_EDGE",EDGE,{"disambiguationData":[OSD([sQuery(id+"F6.wireOp",EDGE,"E71"),sQuery(id+"F6.wireOp",EDGE,"E76.trimOffspring")])]})}),makeQuery(id+"F3.opShell","OFFSET_FACE",FACE,{"disambiguationData":[OSD([sQuery(id+"F0.wireOp",EDGE,"E2"),sQuery(id+"F0.wireOp",EDGE,"E3"),sQuery(id+"F0.wireOp",EDGE,"E4"),sQuery(id+"F0.wireOp",EDGE,"E5")])]})],"blendedInto":[makeQuery(id+"F3.opShell","OFFSET_FACE",FACE,{"disambiguationData":[OSD([sQuery(id+"F0.wireOp",EDGE,"E2"),sQuery(id+"F0.wireOp",EDGE,"E3"),sQuery(id+"F0.wireOp",EDGE,"E4"),sQuery(id+"F0.wireOp",EDGE,"E5")])]})]});
            var Q2;
            Q2=makeQuery(id+"F8.opFillet","BLEND_EDGE",EDGE,{"blendedFrom":[makeQuery(id+"F7.boolean.opBoolean","COPY",EDGE,{"derivedFrom":makeQuery(id+"F7.opExtrude","SWEPT_EDGE",EDGE,{"disambiguationData":[OSD([sQuery(id+"F6.wireOp",EDGE,"E69"),sQuery(id+"F6.wireOp",EDGE,"E73.trimOffspring")])]})}),makeQuery(id+"F3.opShell","OFFSET_FACE",FACE,{"disambiguationData":[OSD([sQuery(id+"F0.wireOp",EDGE,"E2"),sQuery(id+"F0.wireOp",EDGE,"E3"),sQuery(id+"F0.wireOp",EDGE,"E4"),sQuery(id+"F0.wireOp",EDGE,"E5")])]})],"blendedInto":[makeQuery(id+"F3.opShell","OFFSET_FACE",FACE,{"disambiguationData":[OSD([sQuery(id+"F0.wireOp",EDGE,"E2"),sQuery(id+"F0.wireOp",EDGE,"E3"),sQuery(id+"F0.wireOp",EDGE,"E4"),sQuery(id+"F0.wireOp",EDGE,"E5")])]})]});
            var Q3;
            Q3=makeQuery(id+"F8.opFillet","BLEND_EDGE",EDGE,{"blendedFrom":[makeQuery(id+"F7.boolean.opBoolean","COPY",EDGE,{"derivedFrom":makeQuery(id+"F7.opExtrude","SWEPT_EDGE",EDGE,{"disambiguationData":[OSD([sQuery(id+"F6.wireOp",EDGE,"E64"),sQuery(id+"F6.wireOp",EDGE,"E69")])]})}),makeQuery(id+"F1.opExtrude","CAP_FACE",FACE,{"disambiguationData":[OSD([sQuery(id+"F0.wireOp",EDGE,"E2"),sQuery(id+"F0.wireOp",EDGE,"E3"),sQuery(id+"F0.wireOp",EDGE,"E4"),sQuery(id+"F0.wireOp",EDGE,"E5")])],"isStart":true})],"blendedInto":[makeQuery(id+"F1.opExtrude","CAP_FACE",FACE,{"disambiguationData":[OSD([sQuery(id+"F0.wireOp",EDGE,"E2"),sQuery(id+"F0.wireOp",EDGE,"E3"),sQuery(id+"F0.wireOp",EDGE,"E4"),sQuery(id+"F0.wireOp",EDGE,"E5")])],"isStart":true})]});
            var Q4;
            Q4=makeQuery(id+"F8.opFillet","BLEND_EDGE",EDGE,{"blendedFrom":[makeQuery(id+"F7.boolean.opBoolean","COPY",EDGE,{"derivedFrom":makeQuery(id+"F7.opExtrude","SWEPT_EDGE",EDGE,{"disambiguationData":[OSD([sQuery(id+"F6.wireOp",EDGE,"E70"),sQuery(id+"F6.wireOp",EDGE,"E74.trimOffspring")])]})}),makeQuery(id+"F1.opExtrude","CAP_FACE",FACE,{"disambiguationData":[OSD([sQuery(id+"F0.wireOp",EDGE,"E2"),sQuery(id+"F0.wireOp",EDGE,"E3"),sQuery(id+"F0.wireOp",EDGE,"E4"),sQuery(id+"F0.wireOp",EDGE,"E5")])],"isStart":true})],"blendedInto":[makeQuery(id+"F1.opExtrude","CAP_FACE",FACE,{"disambiguationData":[OSD([sQuery(id+"F0.wireOp",EDGE,"E2"),sQuery(id+"F0.wireOp",EDGE,"E3"),sQuery(id+"F0.wireOp",EDGE,"E4"),sQuery(id+"F0.wireOp",EDGE,"E5")])],"isStart":true})]});
            var Q5;
            Q5=makeQuery(id+"F8.opFillet","BLEND_EDGE",EDGE,{"blendedFrom":[makeQuery(id+"F7.boolean.opBoolean","COPY",EDGE,{"derivedFrom":makeQuery(id+"F7.opExtrude","SWEPT_EDGE",EDGE,{"disambiguationData":[OSD([sQuery(id+"F6.wireOp",EDGE,"E72"),sQuery(id+"F6.wireOp",EDGE,"E75.trimOffspring")])]})}),makeQuery(id+"F1.opExtrude","CAP_FACE",FACE,{"disambiguationData":[OSD([sQuery(id+"F0.wireOp",EDGE,"E2"),sQuery(id+"F0.wireOp",EDGE,"E3"),sQuery(id+"F0.wireOp",EDGE,"E4"),sQuery(id+"F0.wireOp",EDGE,"E5")])],"isStart":true})],"blendedInto":[makeQuery(id+"F1.opExtrude","CAP_FACE",FACE,{"disambiguationData":[OSD([sQuery(id+"F0.wireOp",EDGE,"E2"),sQuery(id+"F0.wireOp",EDGE,"E3"),sQuery(id+"F0.wireOp",EDGE,"E4"),sQuery(id+"F0.wireOp",EDGE,"E5")])],"isStart":true})]});
            var Q6;
            Q6=makeQuery(id+"F1.opExtrude","CAP_EDGE",EDGE,{"disambiguationData":[OSD([sQuery(id+"F0.wireOp",EDGE,"E2")])],"isStart":true});
            chamfer(context, id + "F13", {"entities" : qUnion([Q0, Q1, Q2, Q3, Q4, Q5, Q6]), "width" : 1.27 * mm, "tangentPropagation" : true});
        }
        {
            var Q0;
            Q0=makeQuery(id+"F5.boolean.opBoolean","INTERSECT",EDGE,{"derivedFrom":[makeQuery(id+"F1.opExtrude","SWEPT_FACE",FACE,{"disambiguationData":[OSD([sQuery(id+"F0.wireOp",EDGE,"E3")])]}),makeQuery(id+"F5.opExtrude","SWEPT_FACE",FACE,{"disambiguationData":[OSD([sQuery(id+"F4.wireOp",EDGE,"E25")])]})]});
            var Q1;
            Q1=makeQuery(id+"F9.opFillet","BLEND_EDGE",EDGE,{"blendedFrom":[makeQuery(id+"F3.opShell","OFFSET_EDGE",EDGE,{"disambiguationData":[OSD([sQuery(id+"F0.wireOp",EDGE,"E2"),sQuery(id+"F0.wireOp",EDGE,"E3")])]}),makeQuery(id+"F5.boolean.opBoolean","COPY",FACE,{"derivedFrom":makeQuery(id+"F5.opExtrude","SWEPT_FACE",FACE,{"disambiguationData":[OSD([sQuery(id+"F4.wireOp",EDGE,"E25")])]})})],"blendedInto":[makeQuery(id+"F5.boolean.opBoolean","COPY",FACE,{"derivedFrom":makeQuery(id+"F5.opExtrude","SWEPT_FACE",FACE,{"disambiguationData":[OSD([sQuery(id+"F4.wireOp",EDGE,"E25")])]})})]});
            var Q2;
            Q2=makeQuery(id+"F5.boolean.opBoolean","INTERSECT",EDGE,{"derivedFrom":[makeQuery(id+"F1.opExtrude","SWEPT_FACE",FACE,{"disambiguationData":[OSD([sQuery(id+"F0.wireOp",EDGE,"E3")])]}),makeQuery(id+"F5.opExtrude","SWEPT_FACE",FACE,{"disambiguationData":[OSD([sQuery(id+"F4.wireOp",EDGE,"E29")])]})]});
            var Q3;
            Q3=makeQuery(id+"F9.opFillet","BLEND_EDGE",EDGE,{"blendedFrom":[makeQuery(id+"F3.opShell","OFFSET_EDGE",EDGE,{"disambiguationData":[OSD([sQuery(id+"F0.wireOp",EDGE,"E3"),sQuery(id+"F0.wireOp",EDGE,"E4")])]}),makeQuery(id+"F5.boolean.opBoolean","COPY",FACE,{"derivedFrom":makeQuery(id+"F5.opExtrude","SWEPT_FACE",FACE,{"disambiguationData":[OSD([sQuery(id+"F4.wireOp",EDGE,"E29")])]})})],"blendedInto":[makeQuery(id+"F5.boolean.opBoolean","COPY",FACE,{"derivedFrom":makeQuery(id+"F5.opExtrude","SWEPT_FACE",FACE,{"disambiguationData":[OSD([sQuery(id+"F4.wireOp",EDGE,"E29")])]})})]});
            chamfer(context, id + "F14", {"entities" : qUnion([Q0, Q1, Q2, Q3]), "width" : 0.64 * mm, "tangentPropagation" : true});
        }
    });
